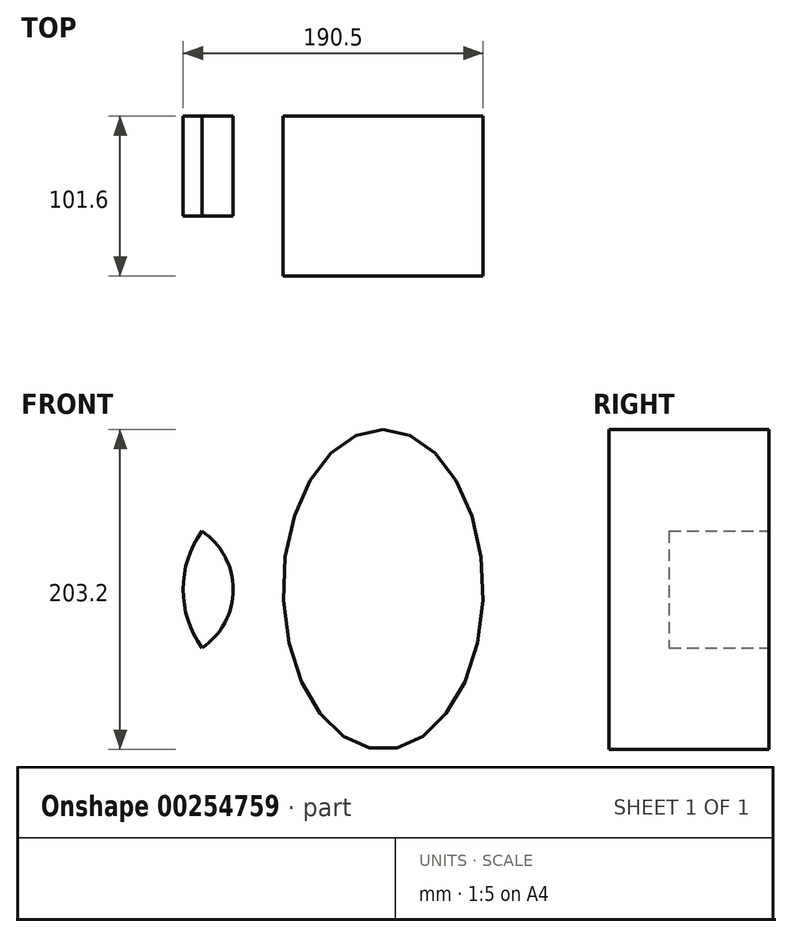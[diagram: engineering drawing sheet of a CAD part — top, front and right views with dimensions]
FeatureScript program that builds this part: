
annotation { "Feature Type Name" : "Feature", "Feature Type Description" : "" }
export const myFeature = defineFeature(function(context is Context, id is Id, definition is map)
    precondition{}
    {
        {
            var Q0;
            Q0=qCreatedBy(makeId("Front.planeOp"),FACE);
            var sketch = newSketch(context, id + "F0", { "sketchPlane" : qUnion([Q0])});
            skLineSegment(sketch, "E0", {"start": v(0, 0) * mm, "end": v(-76.2, 0) * mm});
            skCircle(sketch, "E1", {"center": v(-76.2, 0) * mm, "radius": 44.45 * mm});
            skPoint(sketch, "E2", {"position": v(-31.75, 0) * mm});
            skLineSegment(sketch, "E3", {"start": v(-31.75, 0) * mm, "end": v(-63.5, 0) * mm});
            skCircle(sketch, "E4", {"center": v(0, 0) * mm, "radius": 63.5 * mm});
            skEllipse(sketch, "E5", {"center": v(63.5, 0) * mm, "majorRadius": 101.6 * mm, "minorRadius": 63.5 * mm, "majorAxis": v(0, 1)});
            skSolve(sketch);
        }
        {
            var Q0;
            {var subQ0=sQuery(id+"F0.wireOp",EDGE,"E4");var subQ1=sQuery(id+"F0.wireOp",EDGE,"E1");var subQ2=makeQuery(id+"F0.imprint","INTERSECT",VERTEX,{"disambiguationData":[OD(0.0)],"derivedFrom":[subQ1,subQ0]});Q0=makeQuery(id+"F0.imprint","IMPRINT",FACE,{"disambiguationData":[TD([[makeQuery(id+"F0.imprint","IMPRINT",EDGE,{"disambiguationData":[TD([[subQ2,-1.0]])],"derivedFrom":subQ1}),1.0]])]});}
            extrude(context, id + "F1", {"entities" : qUnion([Q0]), "depth" : 25.4 * mm});
        }
        {
            var Q0;
            {var subQ0=sQuery(id+"F0.wireOp",EDGE,"E3");Q0=makeQuery(id+"F0.imprint","IMPRINT",FACE,{"disambiguationData":[TD([[makeQuery(id+"F0.imprint","IMPRINT",EDGE,{"derivedFrom":subQ0}),-1.0]])]});}
            var Q1;
            {var subQ0=sQuery(id+"F0.wireOp",EDGE,"E3");Q1=makeQuery(id+"F0.imprint","IMPRINT",FACE,{"disambiguationData":[TD([[makeQuery(id+"F0.imprint","IMPRINT",EDGE,{"derivedFrom":subQ0}),1.0]])]});}
            var Q2;
            {var subQ3=sQuery(id+"F0.wireOp",EDGE,"E1");var subQ5=sQuery(id+"F0.wireOp",EDGE,"E4");var subQ6=makeQuery(id+"F0.imprint","INTERSECT",VERTEX,{"disambiguationData":[OD(0.0)],"derivedFrom":[subQ3,subQ5]});Q2=makeQuery(id+"F0.imprint","IMPRINT",FACE,{"disambiguationData":[TD([[makeQuery(id+"F0.imprint","IMPRINT",EDGE,{"disambiguationData":[TD([[subQ6,1.0]])],"derivedFrom":subQ5}),1.0]])]});}
            var Q3;
            {var subQ3=sQuery(id+"F0.wireOp",EDGE,"E1");var subQ5=sQuery(id+"F0.wireOp",EDGE,"E4");var subQ6=makeQuery(id+"F0.imprint","INTERSECT",VERTEX,{"disambiguationData":[OD(1.0)],"derivedFrom":[subQ3,subQ5]});Q3=makeQuery(id+"F0.imprint","IMPRINT",FACE,{"disambiguationData":[TD([[makeQuery(id+"F0.imprint","IMPRINT",EDGE,{"disambiguationData":[TD([[subQ6,-1.0]])],"derivedFrom":subQ5}),1.0]])]});}
            extrude(context, id + "F2", {"entities" : qUnion([Q0, Q1, Q2, Q3]), "operationType" : NewBodyOperationType.ADD, "depth" : 63.5 * mm});
        }
        {
            var Q0;
            {var subQ0=sQuery(id+"F0.wireOp",EDGE,"E5");var subQ1=sQuery(id+"F0.wireOp",EDGE,"E4");var subQ2=makeQuery(id+"F0.imprint","INTERSECT",VERTEX,{"disambiguationData":[OD(0.0)],"derivedFrom":[subQ1,subQ0]});Q0=makeQuery(id+"F0.imprint","IMPRINT",FACE,{"disambiguationData":[TD([[makeQuery(id+"F0.imprint","IMPRINT",EDGE,{"disambiguationData":[TD([[subQ2,1.0]])],"derivedFrom":subQ1}),1.0]])]});}
            var Q1;
            {var subQ0=sQuery(id+"F0.wireOp",EDGE,"E5");var subQ1=sQuery(id+"F0.wireOp",EDGE,"E4");var subQ2=makeQuery(id+"F0.imprint","INTERSECT",VERTEX,{"disambiguationData":[OD(0.0)],"derivedFrom":[subQ1,subQ0]});Q1=makeQuery(id+"F0.imprint","IMPRINT",FACE,{"disambiguationData":[TD([[makeQuery(id+"F0.imprint","IMPRINT",EDGE,{"disambiguationData":[TD([[subQ2,1.0]])],"derivedFrom":subQ1}),-1.0]])]});}
            extrude(context, id + "F3", {"entities" : qUnion([Q0, Q1]), "operationType" : NewBodyOperationType.ADD, "depth" : 101.6 * mm});
        }
    });
